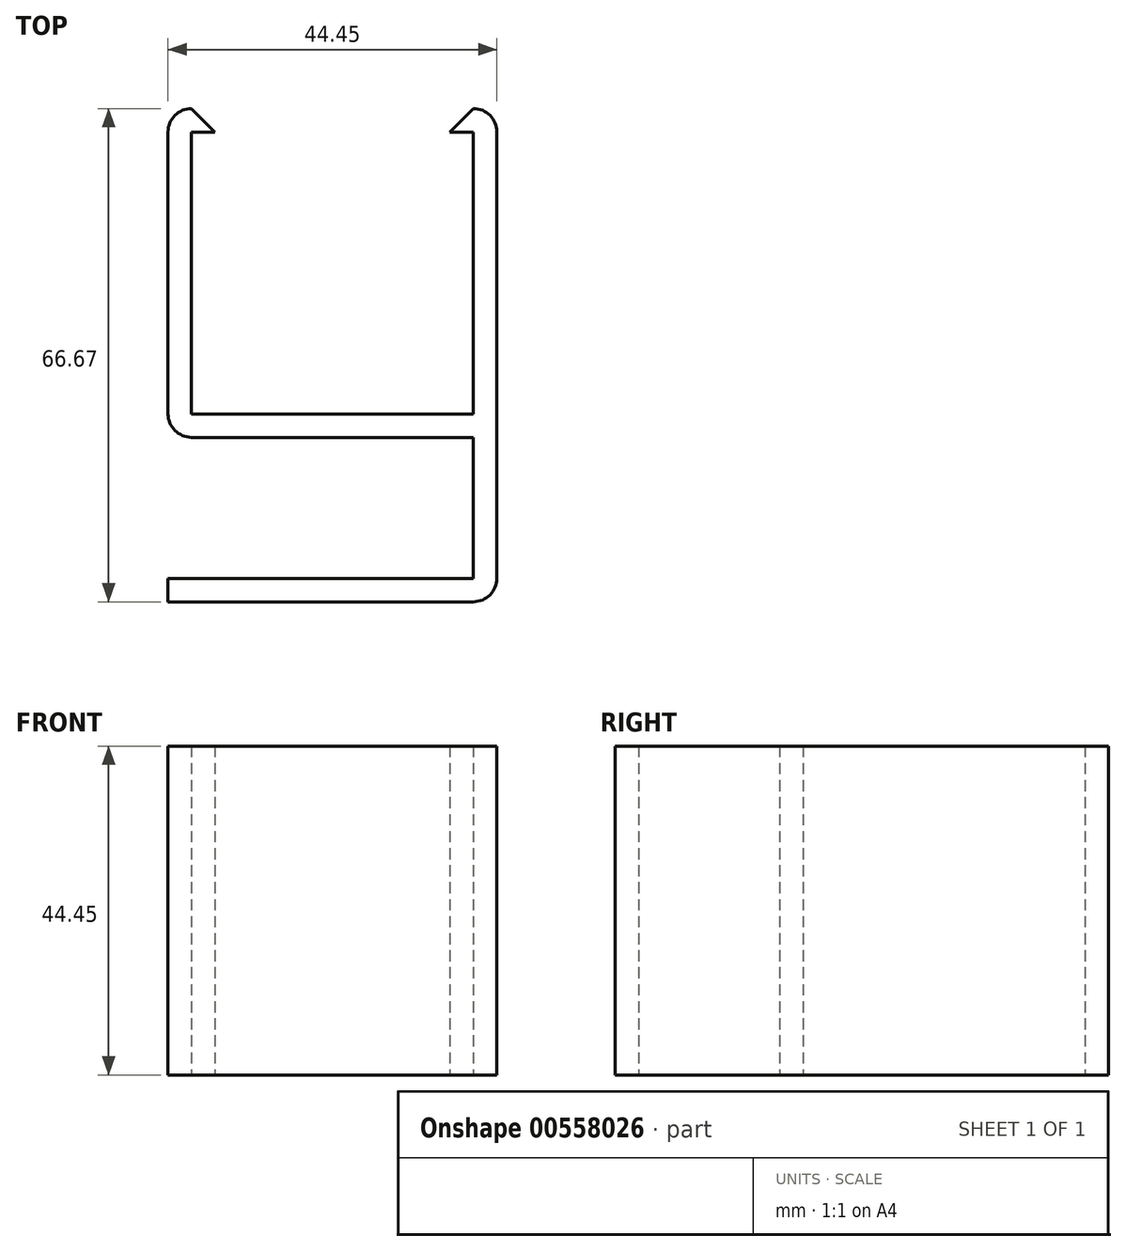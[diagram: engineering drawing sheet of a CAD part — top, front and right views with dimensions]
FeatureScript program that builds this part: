
annotation { "Feature Type Name" : "Feature", "Feature Type Description" : "" }
export const myFeature = defineFeature(function(context is Context, id is Id, definition is map)
    precondition{}
    {
        {
            var Q0;
            Q0=qCreatedBy(makeId("Top.planeOp"),FACE);
            var sketch = newSketch(context, id + "F0", { "sketchPlane" : qUnion([Q0])});
            skLineSegment(sketch, "E0", {"start": v(0, 0) * mm, "end": v(0, 38.1) * mm});
            skLineSegment(sketch, "E1", {"start": v(0, 38.1) * mm, "end": v(3.18, 38.1) * mm});
            skLineSegment(sketch, "E2", {"start": v(-3.18, 38.1) * mm, "end": v(-3.17, 0) * mm});
            skLineSegment(sketch, "E3", {"start": v(41.28, -3.18) * mm, "end": v(41.28, 38.1) * mm});
            skLineSegment(sketch, "E4", {"start": v(38.1, 41.27) * mm, "end": v(38.1, 41.27) * mm});
            skLineSegment(sketch, "E5", {"start": v(38.1, 0) * mm, "end": v(0, 0) * mm});
            skLineSegment(sketch, "E6", {"start": v(34.93, 38.1) * mm, "end": v(38.1, 38.1) * mm});
            skLineSegment(sketch, "E7", {"start": v(38.1, 0) * mm, "end": v(38.1, 38.1) * mm});
            skLineSegment(sketch, "E8", {"start": v(38.1, -22.22) * mm, "end": v(-3.18, -22.23) * mm});
            skLineSegment(sketch, "E9", {"start": v(-3.18, -22.23) * mm, "end": v(-3.18, -25.4) * mm});
            skLineSegment(sketch, "E10", {"start": v(-3.18, -25.4) * mm, "end": v(38.1, -25.4) * mm});
            skLineSegment(sketch, "E11", {"start": v(41.28, -22.23) * mm, "end": v(41.28, -3.18) * mm});
            skLineSegment(sketch, "E12", {"start": v(38.1, -22.22) * mm, "end": v(38.1, -3.18) * mm});
            skLineSegment(sketch, "E13", {"start": v(38.1, -3.18) * mm, "end": v(0, -3.18) * mm});
            skLineSegment(sketch, "E14", {"start": v(3.17, 38.1) * mm, "end": v(0, 41.27) * mm});
            skLineSegment(sketch, "E15", {"start": v(34.93, 38.1) * mm, "end": v(38.1, 41.27) * mm});
            skLineSegment(sketch, "E16", {"start": v(0, 41.27) * mm, "end": v(0, 41.27) * mm});
            skPoint(sketch, "E17.visualSharp", {"position": v(-3.17, -3.18) * mm});
            skArc(sketch, "E17.filletArc", {"start": v(-3.17, 0) * mm, "mid": v(-2.25, -2.25) * mm, "end": v(0, -3.18) * mm});
            skPoint(sketch, "E18.visualSharp", {"position": v(41.27, -25.4) * mm});
            skArc(sketch, "E18.filletArc", {"start": v(38.1, -25.4) * mm, "mid": v(40.35, -24.47) * mm, "end": v(41.28, -22.23) * mm});
            skPoint(sketch, "E19.visualSharp", {"position": v(-3.18, 41.27) * mm});
            skArc(sketch, "E19.filletArc", {"start": v(0, 41.27) * mm, "mid": v(-2.25, 40.35) * mm, "end": v(-3.18, 38.1) * mm});
            skPoint(sketch, "E20.visualSharp", {"position": v(41.28, 41.27) * mm});
            skArc(sketch, "E20.filletArc", {"start": v(41.28, 38.1) * mm, "mid": v(40.35, 40.35) * mm, "end": v(38.1, 41.27) * mm});
            skSolve(sketch);
        }
        {
            var Q0;
            Q0 = qSketchRegion(id + "F0", true);
            extrude(context, id + "F1", {"entities" : qUnion([Q0]), "depth" : 44.45 * mm, "offsetDistance" : 25.4 * mm});
        }
    });
